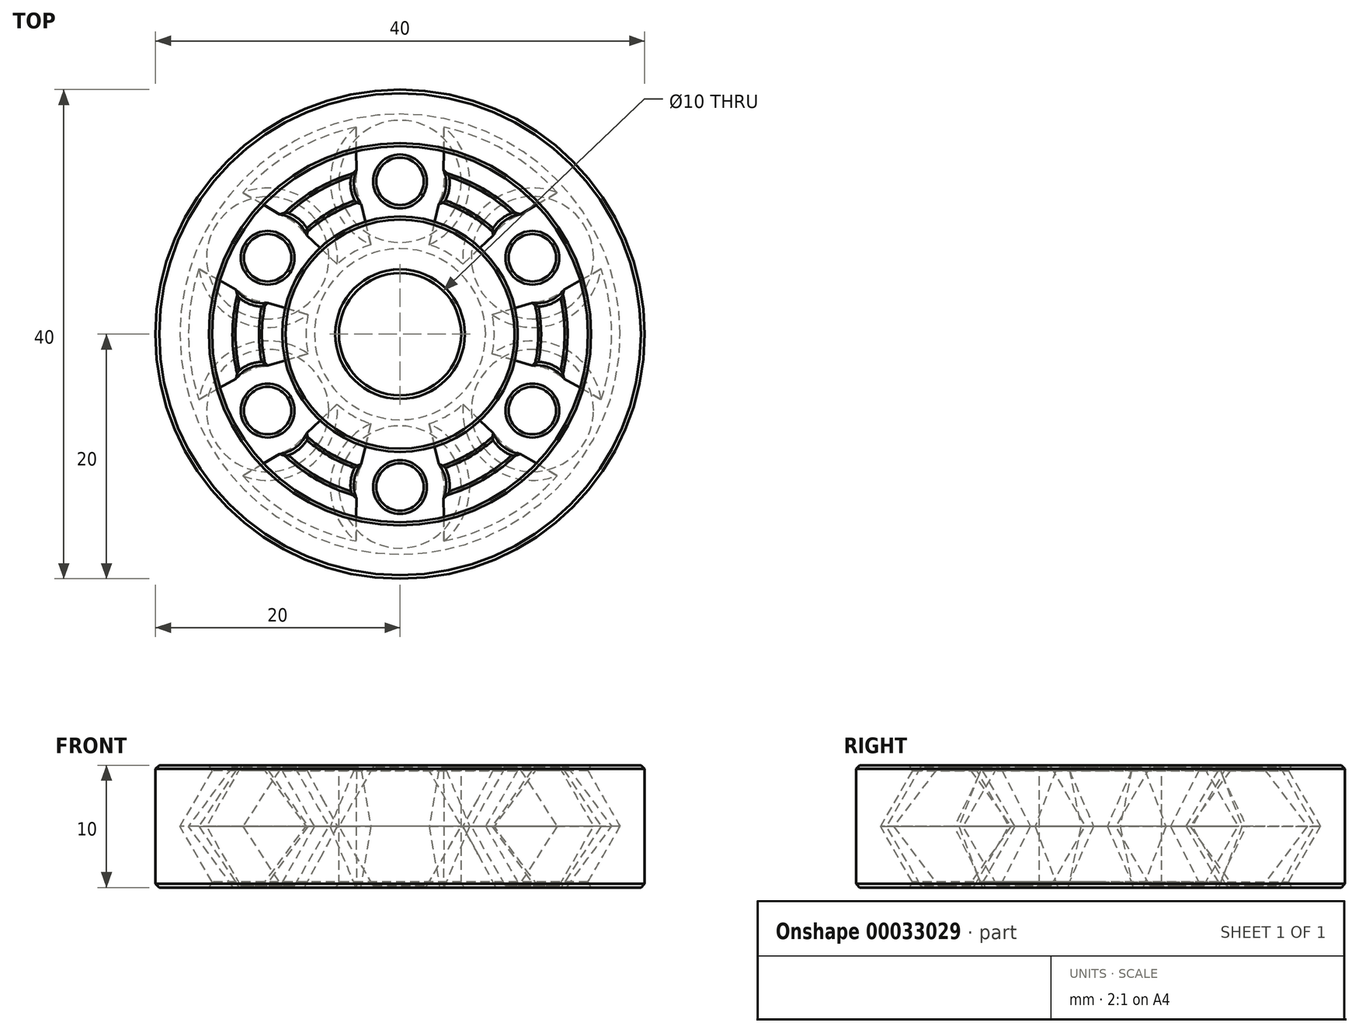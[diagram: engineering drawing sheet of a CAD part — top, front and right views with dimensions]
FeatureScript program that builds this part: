
annotation { "Feature Type Name" : "Feature", "Feature Type Description" : "" }
export const myFeature = defineFeature(function(context is Context, id is Id, definition is map)
    precondition{}
    {
        {
            var Q0;
            Q0=qCreatedBy(makeId("Top.planeOp"),FACE);
            var sketch = newSketch(context, id + "F0", { "sketchPlane" : qUnion([Q0])});
            skCircle(sketch, "E0", {"center": v(0, 0) * mm, "radius": 5 * mm});
            skCircle(sketch, "E1", {"center": v(0, 0) * mm, "radius": 20 * mm});
            skSolve(sketch);
        }
        {
            var Q0;
            Q0=qCreatedBy(makeId("Right.planeOp"),FACE);
            var sketch = newSketch(context, id + "F1", { "sketchPlane" : qUnion([Q0])});
            skLineSegment(sketch, "E2", {"start": v(0, 25) * mm, "end": v(0, -25) * mm, "construction": true});
            skSolve(sketch);
        }
        {
            var Q0;
            Q0=qCreatedBy(makeId("Right.planeOp"),FACE);
            var sketch = newSketch(context, id + "F2", { "sketchPlane" : qUnion([Q0])});
            skLineSegment(sketch, "E3", {"start": v(-5, 5) * mm, "end": v(-5, -5) * mm});
            skLineSegment(sketch, "E4", {"start": v(-5, 5) * mm, "end": v(-9.89, 5) * mm});
            skLineSegment(sketch, "E5", {"start": v(-9.89, 5) * mm, "end": v(-7, 0) * mm});
            skLineSegment(sketch, "E6", {"start": v(-7, 0) * mm, "end": v(-9.89, -5) * mm});
            skLineSegment(sketch, "E7", {"start": v(-9.89, -5) * mm, "end": v(-5, -5) * mm});
            skLineSegment(sketch, "E8", {"start": v(-7, 0) * mm, "end": v(-5, 0) * mm, "construction": true});
            skLineSegment(sketch, "E9", {"start": v(-15.11, 5) * mm, "end": v(-20, 5) * mm});
            skLineSegment(sketch, "E10", {"start": v(-20, 5) * mm, "end": v(-20, -5) * mm});
            skLineSegment(sketch, "E11", {"start": v(-20, -5) * mm, "end": v(-15.11, -5) * mm});
            skLineSegment(sketch, "E12", {"start": v(-15.11, -5) * mm, "end": v(-18, 0) * mm});
            skLineSegment(sketch, "E13", {"start": v(-18, 0) * mm, "end": v(-15.11, 5) * mm});
            skLineSegment(sketch, "E14", {"start": v(-14.61, 5) * mm, "end": v(-10.39, 5) * mm});
            skLineSegment(sketch, "E15", {"start": v(-10.39, 5) * mm, "end": v(-7.5, 0) * mm});
            skLineSegment(sketch, "E16", {"start": v(-7.5, 0) * mm, "end": v(-10.39, -5) * mm});
            skLineSegment(sketch, "E17", {"start": v(-10.39, -5) * mm, "end": v(-14.61, -5) * mm});
            skLineSegment(sketch, "E18", {"start": v(-14.61, -5) * mm, "end": v(-17.5, 0) * mm});
            skLineSegment(sketch, "E19", {"start": v(-17.5, 0) * mm, "end": v(-14.61, 5) * mm});
            skLineSegment(sketch, "E20", {"start": v(-15.11, 5) * mm, "end": v(-14.61, 5) * mm, "construction": true});
            skLineSegment(sketch, "E21", {"start": v(-10.39, 5) * mm, "end": v(-9.89, 5) * mm, "construction": true});
            skLineSegment(sketch, "E22", {"start": v(-10.39, -5) * mm, "end": v(-9.89, -5) * mm, "construction": true});
            skLineSegment(sketch, "E23", {"start": v(-15.11, -5) * mm, "end": v(-14.61, -5) * mm, "construction": true});
            skPoint(sketch, "E24", {"position": v(-12.5, 5) * mm});
            skPoint(sketch, "E25", {"position": v(-12.5, -5) * mm});
            skPoint(sketch, "E26", {"position": v(-12.5, 0) * mm});
            skLineSegment(sketch, "E27", {"start": v(-12.5, 10) * mm, "end": v(-12.5, -10) * mm, "construction": true});
            skSolve(sketch);
        }
        {
            var Q0;
            Q0=qCreatedBy(makeId("Right.planeOp"),FACE);
            var sketch = newSketch(context, id + "F3", { "sketchPlane" : qUnion([Q0])});
            skLineSegment(sketch, "E28.0", {"start": v(-9.89, 5) * mm, "end": v(-7, 0) * mm});
            skLineSegment(sketch, "E28.1", {"start": v(-5, 5) * mm, "end": v(-9.89, 5) * mm});
            skLineSegment(sketch, "E28.2", {"start": v(-5, 5) * mm, "end": v(-5, -5) * mm});
            skLineSegment(sketch, "E28.3", {"start": v(-7, 0) * mm, "end": v(-9.89, -5) * mm});
            skLineSegment(sketch, "E28.4", {"start": v(-9.89, -5) * mm, "end": v(-5, -5) * mm});
            skLineSegment(sketch, "E28.5", {"start": v(-15.11, -5) * mm, "end": v(-18, 0) * mm});
            skLineSegment(sketch, "E28.6", {"start": v(-18, 0) * mm, "end": v(-15.11, 5) * mm});
            skLineSegment(sketch, "E28.7", {"start": v(-15.11, 5) * mm, "end": v(-20, 5) * mm});
            skLineSegment(sketch, "E28.8", {"start": v(-20, 5) * mm, "end": v(-20, -5) * mm});
            skLineSegment(sketch, "E28.9", {"start": v(-20, -5) * mm, "end": v(-15.11, -5) * mm});
            skSolve(sketch);
        }
        {
            var Q0;
            Q0 = qSketchRegion(id + "F3", true);
            var Q1;
            Q1=sQuery(id+"F1.wireOp",EDGE,"E2");
            revolve(context, id + "F4", {"entities" : qUnion([Q0]), "axis" : qUnion([Q1]), "revolveType" : RevolveType.FULL});
        }
        {
            var Q0;
            Q0=qCreatedBy(makeId("Right.planeOp"),FACE);
            var sketch = newSketch(context, id + "F5", { "sketchPlane" : qUnion([Q0])});
            skLineSegment(sketch, "E29.0", {"start": v(-17.5, 0) * mm, "end": v(-14.61, 5) * mm});
            skLineSegment(sketch, "E29.1", {"start": v(-14.61, 5) * mm, "end": v(-12.5, 5) * mm});
            skLineSegment(sketch, "E29.2", {"start": v(-14.61, -5) * mm, "end": v(-17.5, 0) * mm});
            skLineSegment(sketch, "E29.3", {"start": v(-12.5, -5) * mm, "end": v(-14.61, -5) * mm});
            skLineSegment(sketch, "E30", {"start": v(-12.5, 5) * mm, "end": v(-12.5, -5) * mm});
            skPoint(sketch, "E31.orphan", {"position": v(-10.39, 5) * mm});
            skPoint(sketch, "E32.orphan", {"position": v(-10.39, -5) * mm});
            skSolve(sketch);
        }
        {
            var Q0;
            Q0 = qSketchRegion(id + "F5", true);
            var Q1;
            Q1=sQuery(id+"F2.wireOp",EDGE,"E27");
            revolve(context, id + "F6", {"entities" : qUnion([Q0]), "axis" : qUnion([Q1]), "revolveType" : RevolveType.FULL});
        }
        {
            var Q0;
            Q0=makeQuery(id+"F6.opRevolve","SWEPT_BODY",BODY,{"disambiguationData":[OSD([sQuery(id+"F5.wireOp",EDGE,"E29.0"),sQuery(id+"F5.wireOp",EDGE,"E29.1"),sQuery(id+"F5.wireOp",EDGE,"E29.2"),sQuery(id+"F5.wireOp",EDGE,"E29.3"),sQuery(id+"F5.wireOp",EDGE,"E30")])]});
            var Q1;
            Q1=sQuery(id+"F1.wireOp",EDGE,"E2");
            circularPattern(context, id + "F7", {"entities" : qUnion([Q0]), "axis" : qUnion([Q1]), "angle" : 60 * degree, "instanceCount" : 6});
        }
        {
            var Q0;
            Q0=qCreatedBy(makeId("Top.planeOp"),FACE);
            var sketch = newSketch(context, id + "F8", { "sketchPlane" : qUnion([Q0])});
            skCircle(sketch, "E33.0", {"center": v(10.83, 6.25) * mm, "radius": 5 * mm, "construction": true});
            skArc(sketch, "E34", {"start": v(7.53, -1.6) * mm, "mid": v(7.7, 0) * mm, "end": v(7.53, 1.6) * mm});
            skArc(sketch, "E35.trimOffspring", {"start": v(7.53, 1.6) * mm, "mid": v(13.03, 1) * mm, "end": v(16.45, 5.35) * mm});
            skArc(sketch, "E36.trimOffspring", {"start": v(16.45, -5.35) * mm, "mid": v(13.03, -1) * mm, "end": v(7.53, -1.6) * mm});
            skArc(sketch, "E37.trimOffspring", {"start": v(16.45, -5.35) * mm, "mid": v(17.3, 0) * mm, "end": v(16.45, 5.35) * mm});
            skSolve(sketch);
        }
        {
            var Q0;
            Q0=makeQuery(id+"F4.opRevolve","SWEPT_FACE",FACE,{"disambiguationData":[OSD([sQuery(id+"F3.wireOp",EDGE,"E28.1")])]});
            var sketch = newSketch(context, id + "F9", { "sketchPlane" : qUnion([Q0])});
            skArc(sketch, "E38.0", {"start": v(11.08, -2.65) * mm, "mid": v(11.39, 0) * mm, "end": v(11.08, 2.65) * mm});
            skArc(sketch, "E39.0", {"start": v(11.08, 2.65) * mm, "mid": v(12.18, 2.9) * mm, "end": v(13.16, 3.5) * mm});
            skArc(sketch, "E40.0", {"start": v(13.16, -3.5) * mm, "mid": v(12.18, -2.9) * mm, "end": v(11.08, -2.65) * mm});
            skArc(sketch, "E41.0", {"start": v(13.16, -3.5) * mm, "mid": v(13.61, 0) * mm, "end": v(13.16, 3.5) * mm});
            skSolve(sketch);
        }
        {
            var Q0;
            Q0=makeQuery(id+"F4.opRevolve","SWEPT_FACE",FACE,{"disambiguationData":[OSD([sQuery(id+"F3.wireOp",EDGE,"E28.9")])]});
            var sketch = newSketch(context, id + "F10", { "sketchPlane" : qUnion([Q0])});
            skArc(sketch, "E42.0", {"start": v(13.16, 3.5) * mm, "mid": v(13.61, 0) * mm, "end": v(13.16, -3.5) * mm});
            skArc(sketch, "E42.1", {"start": v(11.08, -2.65) * mm, "mid": v(12.18, -2.9) * mm, "end": v(13.16, -3.5) * mm});
            skArc(sketch, "E42.2", {"start": v(11.08, 2.65) * mm, "mid": v(11.39, 0) * mm, "end": v(11.08, -2.65) * mm});
            skArc(sketch, "E42.3", {"start": v(13.16, 3.5) * mm, "mid": v(12.18, 2.9) * mm, "end": v(11.08, 2.65) * mm});
            skSolve(sketch);
        }
        {
            var Q0;
            Q0 = qSketchRegion(id + "F9", true);
            var Q1;
            Q1 = qSketchRegion(id + "F8", true);
            loft(context, id + "F11", {"sheetProfilesArray" : [{ "sheetProfileEntities" : qUnion([Q0]) }, { "sheetProfileEntities" : qUnion([Q1]) }]});
        }
        {
            var Q1;
            Q1 = qSketchRegion(id + "F8", true);
            var Q2;
            Q2 = qSketchRegion(id + "F10", true);
            loft(context, id + "F12", {"operationType" : NewBodyOperationType.ADD, "sheetProfilesArray" : [{ "sheetProfileEntities" : qUnion([Q1]) }, { "sheetProfileEntities" : qUnion([Q2]) }]});
        }
        {
            var Q0;
            Q0=makeQuery(id+"F11.opLoft","SWEPT_BODY",BODY,{"disambiguationData":[OSD([makeQuery(id+"F8.imprint","IMPRINT",FACE,{"disambiguationData":[TD([[makeQuery(id+"F8.imprint","IMPRINT",EDGE,{"derivedFrom":sQuery(id+"F8.wireOp",EDGE,"E34")}),-1.0]])]}),makeQuery(id+"F9.imprint","IMPRINT",FACE,{"disambiguationData":[TD([[makeQuery(id+"F9.imprint","IMPRINT",EDGE,{"derivedFrom":sQuery(id+"F9.wireOp",EDGE,"E38.0")}),-1.0]])]})])]});
            var Q1;
            Q1=sQuery(id+"F1.wireOp",EDGE,"E2");
            circularPattern(context, id + "F13", {"entities" : qUnion([Q0]), "axis" : qUnion([Q1]), "angle" : 60 * degree, "instanceCount" : 6});
        }
        {
            var Q0;
            Q0=makeQuery(id+"F4.opRevolve","SWEPT_FACE",FACE,{"disambiguationData":[OSD([sQuery(id+"F3.wireOp",EDGE,"E28.7")])]});
            var Q1;
            Q1=makeQuery(id+"F4.opRevolve","SWEPT_FACE",FACE,{"disambiguationData":[OSD([sQuery(id+"F3.wireOp",EDGE,"E28.1")])]});
            var Q2;
            Q2=makeQuery(id+"F13.opPattern","COPY",FACE,{"derivedFrom":makeQuery(id+"F11.opLoft","CAP_FACE",FACE,{"disambiguationData":[OSD([makeQuery(id+"F9.imprint","IMPRINT",FACE,{"disambiguationData":[TD([[makeQuery(id+"F9.imprint","IMPRINT",EDGE,{"derivedFrom":sQuery(id+"F9.wireOp",EDGE,"E38.0")}),-1.0]])]})])],"isStart":true}),"instanceName":"1"});
            var Q3;
            Q3=makeQuery(id+"F7.opPattern","COPY",FACE,{"derivedFrom":makeQuery(id+"F6.opRevolve","SWEPT_FACE",FACE,{"disambiguationData":[OSD([sQuery(id+"F5.wireOp",EDGE,"E29.1")])]}),"instanceName":"5"});
            var Q4;
            Q4=makeQuery(id+"F11.opLoft","CAP_FACE",FACE,{"disambiguationData":[OSD([makeQuery(id+"F9.imprint","IMPRINT",FACE,{"disambiguationData":[TD([[makeQuery(id+"F9.imprint","IMPRINT",EDGE,{"derivedFrom":sQuery(id+"F9.wireOp",EDGE,"E38.0")}),-1.0]])]})])],"isStart":true});
            var Q5;
            Q5=makeQuery(id+"F7.opPattern","COPY",FACE,{"derivedFrom":makeQuery(id+"F6.opRevolve","SWEPT_FACE",FACE,{"disambiguationData":[OSD([sQuery(id+"F5.wireOp",EDGE,"E29.1")])]}),"instanceName":"4"});
            var Q6;
            Q6=makeQuery(id+"F13.opPattern","COPY",FACE,{"derivedFrom":makeQuery(id+"F11.opLoft","CAP_FACE",FACE,{"disambiguationData":[OSD([makeQuery(id+"F9.imprint","IMPRINT",FACE,{"disambiguationData":[TD([[makeQuery(id+"F9.imprint","IMPRINT",EDGE,{"derivedFrom":sQuery(id+"F9.wireOp",EDGE,"E38.0")}),-1.0]])]})])],"isStart":true}),"instanceName":"5"});
            var Q7;
            Q7=makeQuery(id+"F7.opPattern","COPY",FACE,{"derivedFrom":makeQuery(id+"F6.opRevolve","SWEPT_FACE",FACE,{"disambiguationData":[OSD([sQuery(id+"F5.wireOp",EDGE,"E29.1")])]}),"instanceName":"3"});
            var Q8;
            Q8=makeQuery(id+"F13.opPattern","COPY",FACE,{"derivedFrom":makeQuery(id+"F11.opLoft","CAP_FACE",FACE,{"disambiguationData":[OSD([makeQuery(id+"F9.imprint","IMPRINT",FACE,{"disambiguationData":[TD([[makeQuery(id+"F9.imprint","IMPRINT",EDGE,{"derivedFrom":sQuery(id+"F9.wireOp",EDGE,"E38.0")}),-1.0]])]})])],"isStart":true}),"instanceName":"4"});
            var Q9;
            Q9=makeQuery(id+"F7.opPattern","COPY",FACE,{"derivedFrom":makeQuery(id+"F6.opRevolve","SWEPT_FACE",FACE,{"disambiguationData":[OSD([sQuery(id+"F5.wireOp",EDGE,"E29.1")])]}),"instanceName":"2"});
            var Q10;
            Q10=makeQuery(id+"F13.opPattern","COPY",FACE,{"derivedFrom":makeQuery(id+"F11.opLoft","CAP_FACE",FACE,{"disambiguationData":[OSD([makeQuery(id+"F9.imprint","IMPRINT",FACE,{"disambiguationData":[TD([[makeQuery(id+"F9.imprint","IMPRINT",EDGE,{"derivedFrom":sQuery(id+"F9.wireOp",EDGE,"E38.0")}),-1.0]])]})])],"isStart":true}),"instanceName":"3"});
            var Q11;
            Q11=makeQuery(id+"F7.opPattern","COPY",FACE,{"derivedFrom":makeQuery(id+"F6.opRevolve","SWEPT_FACE",FACE,{"disambiguationData":[OSD([sQuery(id+"F5.wireOp",EDGE,"E29.1")])]}),"instanceName":"1"});
            var Q12;
            Q12=makeQuery(id+"F13.opPattern","COPY",FACE,{"derivedFrom":makeQuery(id+"F11.opLoft","CAP_FACE",FACE,{"disambiguationData":[OSD([makeQuery(id+"F9.imprint","IMPRINT",FACE,{"disambiguationData":[TD([[makeQuery(id+"F9.imprint","IMPRINT",EDGE,{"derivedFrom":sQuery(id+"F9.wireOp",EDGE,"E38.0")}),-1.0]])]})])],"isStart":true}),"instanceName":"2"});
            var Q13;
            Q13=makeQuery(id+"F6.opRevolve","SWEPT_FACE",FACE,{"disambiguationData":[OSD([sQuery(id+"F5.wireOp",EDGE,"E29.1")])]});
            var Q14;
            Q14=makeQuery(id+"F4.opRevolve","SWEPT_EDGE",EDGE,{"disambiguationData":[OSD([sQuery(id+"F3.wireOp",EDGE,"E28.8"),sQuery(id+"F3.wireOp",EDGE,"E28.9")])]});
            var Q15;
            Q15=makeQuery(id+"F7.opPattern","COPY",EDGE,{"derivedFrom":makeQuery(id+"F6.opRevolve","SWEPT_EDGE",EDGE,{"disambiguationData":[OSD([sQuery(id+"F5.wireOp",EDGE,"E29.2"),sQuery(id+"F5.wireOp",EDGE,"E29.3")])]}),"instanceName":"5"});
            var Q16;
            Q16=makeQuery(id+"F4.opRevolve","SWEPT_EDGE",EDGE,{"disambiguationData":[OSD([sQuery(id+"F3.wireOp",EDGE,"E28.5"),sQuery(id+"F3.wireOp",EDGE,"E28.9")])]});
            var Q17;
            Q17=makeQuery(id+"F4.opRevolve","SWEPT_FACE",FACE,{"disambiguationData":[OSD([sQuery(id+"F3.wireOp",EDGE,"E28.4")])]});
            var Q18;
            Q18=makeQuery(id+"F12.opLoft","CAP_FACE",FACE,{"disambiguationData":[OSD([makeQuery(id+"F10.imprint","IMPRINT",FACE,{"disambiguationData":[TD([[makeQuery(id+"F10.imprint","IMPRINT",EDGE,{"derivedFrom":sQuery(id+"F10.wireOp",EDGE,"E42.0")}),-1.0]])]})])],"isStart":true});
            var Q19;
            Q19=makeQuery(id+"F7.opPattern","COPY",FACE,{"derivedFrom":makeQuery(id+"F6.opRevolve","SWEPT_FACE",FACE,{"disambiguationData":[OSD([sQuery(id+"F5.wireOp",EDGE,"E29.3")])]}),"instanceName":"4"});
            var Q20;
            Q20=makeQuery(id+"F13.opPattern","COPY",FACE,{"derivedFrom":makeQuery(id+"F12.opLoft","CAP_FACE",FACE,{"disambiguationData":[OSD([makeQuery(id+"F10.imprint","IMPRINT",FACE,{"disambiguationData":[TD([[makeQuery(id+"F10.imprint","IMPRINT",EDGE,{"derivedFrom":sQuery(id+"F10.wireOp",EDGE,"E42.0")}),-1.0]])]})])],"isStart":true}),"instanceName":"5"});
            var Q21;
            Q21=makeQuery(id+"F7.opPattern","COPY",FACE,{"derivedFrom":makeQuery(id+"F6.opRevolve","SWEPT_FACE",FACE,{"disambiguationData":[OSD([sQuery(id+"F5.wireOp",EDGE,"E29.3")])]}),"instanceName":"3"});
            var Q22;
            Q22=makeQuery(id+"F13.opPattern","COPY",FACE,{"derivedFrom":makeQuery(id+"F12.opLoft","CAP_FACE",FACE,{"disambiguationData":[OSD([makeQuery(id+"F10.imprint","IMPRINT",FACE,{"disambiguationData":[TD([[makeQuery(id+"F10.imprint","IMPRINT",EDGE,{"derivedFrom":sQuery(id+"F10.wireOp",EDGE,"E42.0")}),-1.0]])]})])],"isStart":true}),"instanceName":"4"});
            var Q23;
            Q23=makeQuery(id+"F7.opPattern","COPY",FACE,{"derivedFrom":makeQuery(id+"F6.opRevolve","SWEPT_FACE",FACE,{"disambiguationData":[OSD([sQuery(id+"F5.wireOp",EDGE,"E29.3")])]}),"instanceName":"2"});
            var Q24;
            Q24=makeQuery(id+"F13.opPattern","COPY",FACE,{"derivedFrom":makeQuery(id+"F12.opLoft","CAP_FACE",FACE,{"disambiguationData":[OSD([makeQuery(id+"F10.imprint","IMPRINT",FACE,{"disambiguationData":[TD([[makeQuery(id+"F10.imprint","IMPRINT",EDGE,{"derivedFrom":sQuery(id+"F10.wireOp",EDGE,"E42.0")}),-1.0]])]})])],"isStart":true}),"instanceName":"3"});
            var Q25;
            Q25=makeQuery(id+"F7.opPattern","COPY",FACE,{"derivedFrom":makeQuery(id+"F6.opRevolve","SWEPT_FACE",FACE,{"disambiguationData":[OSD([sQuery(id+"F5.wireOp",EDGE,"E29.3")])]}),"instanceName":"1"});
            var Q26;
            Q26=makeQuery(id+"F13.opPattern","COPY",FACE,{"derivedFrom":makeQuery(id+"F12.opLoft","CAP_FACE",FACE,{"disambiguationData":[OSD([makeQuery(id+"F10.imprint","IMPRINT",FACE,{"disambiguationData":[TD([[makeQuery(id+"F10.imprint","IMPRINT",EDGE,{"derivedFrom":sQuery(id+"F10.wireOp",EDGE,"E42.0")}),-1.0]])]})])],"isStart":true}),"instanceName":"2"});
            var Q27;
            Q27=makeQuery(id+"F6.opRevolve","SWEPT_FACE",FACE,{"disambiguationData":[OSD([sQuery(id+"F5.wireOp",EDGE,"E29.3")])]});
            chamfer(context, id + "F14", {"entities" : qUnion([Q0, Q1, Q2, Q3, Q4, Q5, Q6, Q7, Q8, Q9, Q10, Q11, Q12, Q13, Q14, Q15, Q16, Q17, Q18, Q19, Q20, Q21, Q22, Q23, Q24, Q25, Q26, Q27]), "width" : 0.3 * mm, "tangentPropagation" : true});
        }
    });
